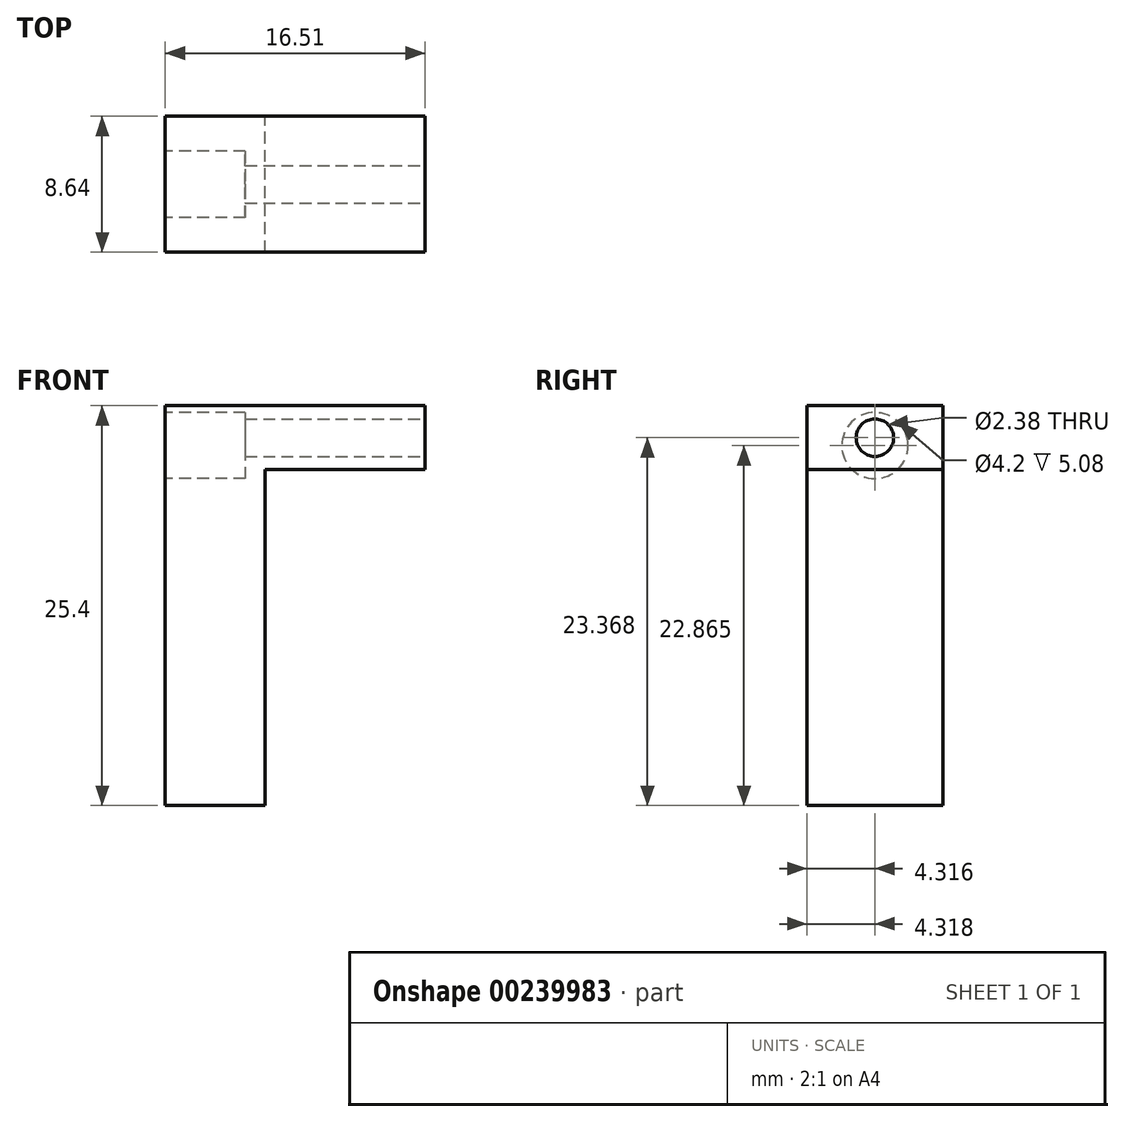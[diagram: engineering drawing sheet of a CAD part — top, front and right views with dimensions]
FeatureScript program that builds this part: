
annotation { "Feature Type Name" : "Feature", "Feature Type Description" : "" }
export const myFeature = defineFeature(function(context is Context, id is Id, definition is map)
    precondition{}
    {
        {
            var Q0;
            Q0=qCreatedBy(makeId("Right.planeOp"),FACE);
            var sketch = newSketch(context, id + "F0", { "sketchPlane" : qUnion([Q0])});
            skLineSegment(sketch, "E0.bottom", {"start": v(0, 0) * mm, "end": v(8.64, 0) * mm});
            skLineSegment(sketch, "E0.top", {"start": v(0, 25.4) * mm, "end": v(8.64, 25.4) * mm});
            skLineSegment(sketch, "E0.left", {"start": v(0, 0) * mm, "end": v(0, 25.4) * mm});
            skLineSegment(sketch, "E0.right", {"start": v(8.64, 0) * mm, "end": v(8.64, 25.4) * mm});
            skSolve(sketch);
        }
        {
            var Q0;
            Q0=makeQuery(id+"F0.imprint","IMPRINT",FACE,{"disambiguationData":[TD([[makeQuery(id+"F0.imprint","IMPRINT",EDGE,{"derivedFrom":sQuery(id+"F0.wireOp",EDGE,"E0.bottom")}),1.0]])]});
            extrude(context, id + "F1", {"entities" : qUnion([Q0]), "depth" : 6.35 * mm});
        }
        {
            var Q0;
            Q0=makeQuery(id+"F1.opExtrude","CAP_FACE",FACE,{"disambiguationData":[OSD([sQuery(id+"F0.wireOp",EDGE,"E0.bottom"),sQuery(id+"F0.wireOp",EDGE,"E0.top"),sQuery(id+"F0.wireOp",EDGE,"E0.left"),sQuery(id+"F0.wireOp",EDGE,"E0.right")])],"isStart":false});
            var sketch = newSketch(context, id + "F2", { "sketchPlane" : qUnion([Q0])});
            skLineSegment(sketch, "E1.bottom", {"start": v(0, 25.4) * mm, "end": v(8.64, 25.4) * mm});
            skLineSegment(sketch, "E1.top", {"start": v(0, 21.34) * mm, "end": v(8.64, 21.34) * mm});
            skLineSegment(sketch, "E1.left", {"start": v(0, 25.4) * mm, "end": v(0, 21.34) * mm});
            skLineSegment(sketch, "E1.right", {"start": v(8.64, 25.4) * mm, "end": v(8.64, 21.34) * mm});
            skSolve(sketch);
        }
        {
            var Q0;
            Q0=makeQuery(id+"F2.imprint","IMPRINT",FACE,{"disambiguationData":[TD([[makeQuery(id+"F2.imprint","IMPRINT",EDGE,{"derivedFrom":sQuery(id+"F2.wireOp",EDGE,"E1.bottom")}),-1.0]])]});
            extrude(context, id + "F3", {"entities" : qUnion([Q0]), "operationType" : NewBodyOperationType.ADD, "depth" : 10.16 * mm});
        }
        {
            var Q0;
            Q0=makeQuery(id+"F3.opExtrude","CAP_FACE",FACE,{"disambiguationData":[OSD([sQuery(id+"F2.wireOp",EDGE,"E1.bottom"),sQuery(id+"F2.wireOp",EDGE,"E1.top"),sQuery(id+"F2.wireOp",EDGE,"E1.left"),sQuery(id+"F2.wireOp",EDGE,"E1.right")])],"isStart":false});
            var sketch = newSketch(context, id + "F4", { "sketchPlane" : qUnion([Q0])});
            skCircle(sketch, "E2", {"center": v(4.32, 23.37) * mm, "radius": 1.2 * mm});
            skPoint(sketch, "E2.centerSnap0", {"position": v(0, 23.37) * mm});
            skPoint(sketch, "E2.centerSnap1", {"position": v(4.32, 25.4) * mm});
            skSolve(sketch);
        }
        {
            var Q0;
            Q0=makeQuery(id+"F4.imprint","IMPRINT",FACE,{"disambiguationData":[TD([[makeQuery(id+"F4.imprint","IMPRINT",EDGE,{"derivedFrom":sQuery(id+"F4.wireOp",EDGE,"E2")}),1.0]])]});
            extrude(context, id + "F5", {"entities" : qUnion([Q0]), "operationType" : NewBodyOperationType.REMOVE, "endBound" : BoundingType.THROUGH_ALL, "oppositeDirection" : true, "depth" : 25.4 * mm});
        }
        {
            var Q0;
            Q0=makeQuery(id+"F1.opExtrude","CAP_FACE",FACE,{"disambiguationData":[OSD([sQuery(id+"F0.wireOp",EDGE,"E0.bottom"),sQuery(id+"F0.wireOp",EDGE,"E0.top"),sQuery(id+"F0.wireOp",EDGE,"E0.left"),sQuery(id+"F0.wireOp",EDGE,"E0.right")])],"isStart":true});
            var sketch = newSketch(context, id + "F6", { "sketchPlane" : qUnion([Q0])});
            skLineSegment(sketch, "E3", {"start": v(-4.32, 25.4) * mm, "end": v(-4.32, 20.15) * mm, "construction": true});
            skLineSegment(sketch, "E4", {"start": v(-4.32, 23.37) * mm, "end": v(-2.1, 23.37) * mm, "construction": true});
            skCircle(sketch, "E5", {"center": v(-4.32, 23.37) * mm, "radius": 2.1 * mm});
            skSolve(sketch);
        }
        {
            var Q0;
            Q0=makeQuery(id+"F6.imprint","IMPRINT",FACE,{"disambiguationData":[TD([[makeQuery(id+"F6.imprint","IMPRINT",EDGE,{"derivedFrom":makeQuery(id+"F1.opExtrude","CAP_EDGE",EDGE,{"disambiguationData":[OSD([sQuery(id+"F0.wireOp",EDGE,"E0.bottom")])],"isStart":true})}),-1.0]])]});
            var sketch = newSketch(context, id + "F7", { "sketchPlane" : qUnion([Q0])});
            skLineSegment(sketch, "E6", {"start": v(-4.32, 23.37) * mm, "end": v(-4.32, 22.86) * mm, "construction": true});
            skCircle(sketch, "E7", {"center": v(-4.32, 22.86) * mm, "radius": 2.1 * mm});
            skSolve(sketch);
        }
        {
            var Q0;
            Q0 = qSketchRegion(id + "F7", true);
            extrude(context, id + "F8", {"entities" : qUnion([Q0]), "operationType" : NewBodyOperationType.REMOVE, "oppositeDirection" : true, "depth" : 5.08 * mm});
        }
    });
